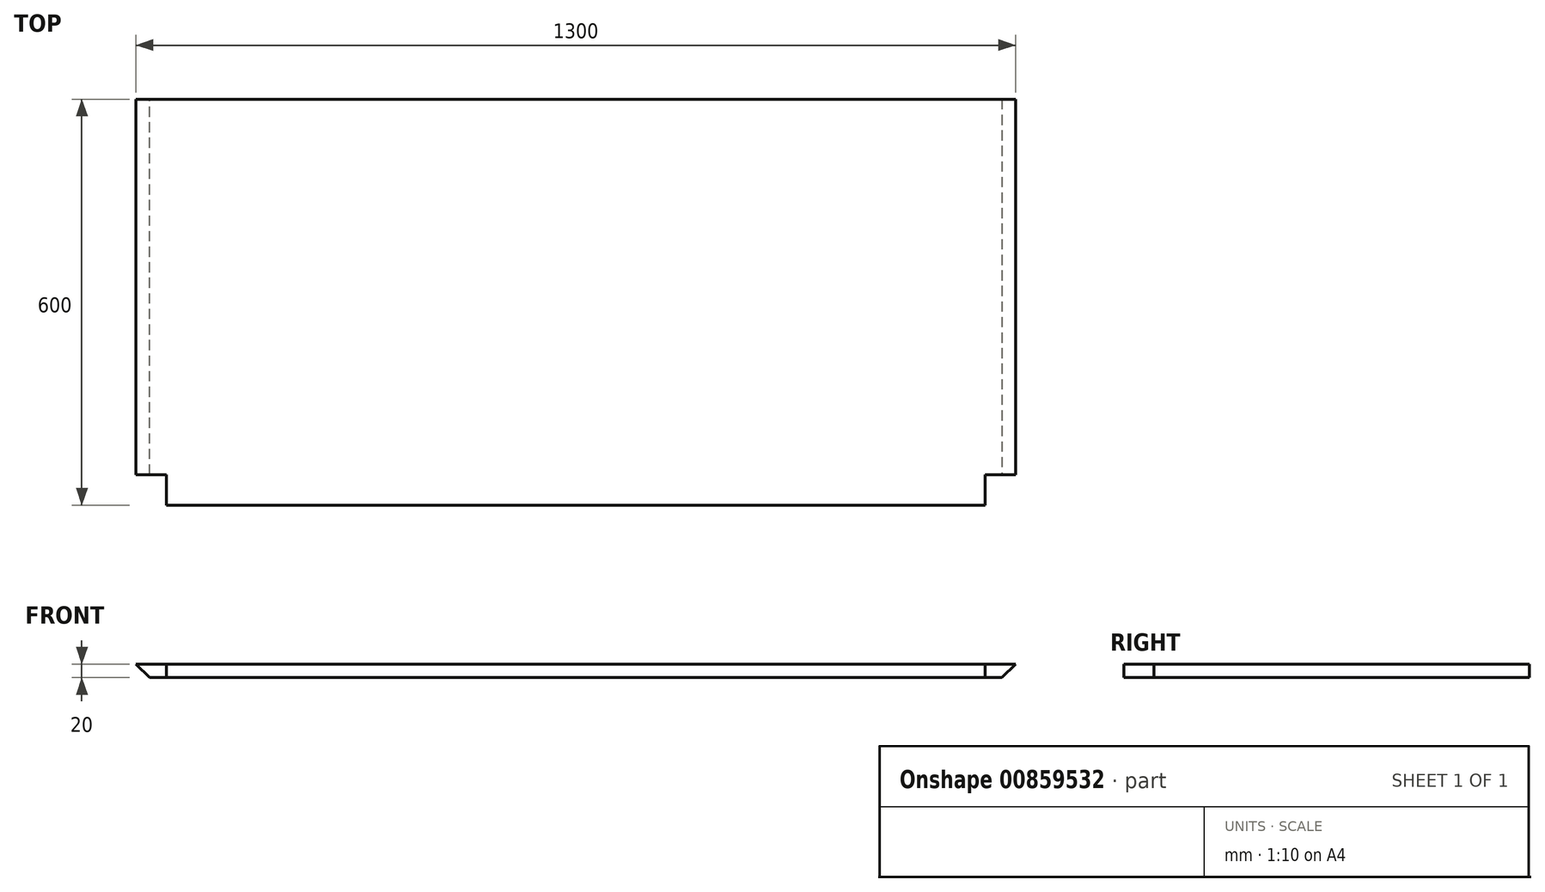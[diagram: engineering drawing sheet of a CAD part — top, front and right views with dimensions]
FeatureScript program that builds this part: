
annotation { "Feature Type Name" : "Feature", "Feature Type Description" : "" }
export const myFeature = defineFeature(function(context is Context, id is Id, definition is map)
    precondition{}
    {
        {
            var Q0;
            Q0=qCreatedBy(makeId("Top.planeOp"),FACE);
            var sketch = newSketch(context, id + "F0", { "sketchPlane" : qUnion([Q0])});
            skLineSegment(sketch, "E0.bottom", {"start": v(-1245.78, 569.46) * mm, "end": v(54.22, 569.46) * mm});
            skLineSegment(sketch, "E0.top", {"start": v(-1245.78, -30.54) * mm, "end": v(54.22, -30.54) * mm});
            skLineSegment(sketch, "E0.left", {"start": v(-1245.78, 569.46) * mm, "end": v(-1245.78, -30.54) * mm});
            skLineSegment(sketch, "E0.right", {"start": v(54.22, 569.46) * mm, "end": v(54.22, -30.54) * mm});
            skLineSegment(sketch, "E1.bottom", {"start": v(-1245.78, -30.54) * mm, "end": v(-1200.78, -30.54) * mm});
            skLineSegment(sketch, "E1.top", {"start": v(-1245.78, 14.46) * mm, "end": v(-1200.78, 14.46) * mm});
            skLineSegment(sketch, "E1.left", {"start": v(-1245.78, -30.54) * mm, "end": v(-1245.78, 14.46) * mm});
            skLineSegment(sketch, "E1.right", {"start": v(-1200.78, -30.54) * mm, "end": v(-1200.78, 14.46) * mm});
            skLineSegment(sketch, "E2.bottom", {"start": v(54.22, -30.54) * mm, "end": v(9.22, -30.54) * mm});
            skLineSegment(sketch, "E2.top", {"start": v(54.22, 14.46) * mm, "end": v(9.22, 14.46) * mm});
            skLineSegment(sketch, "E2.left", {"start": v(54.22, -30.54) * mm, "end": v(54.22, 14.46) * mm});
            skLineSegment(sketch, "E2.right", {"start": v(9.22, -30.54) * mm, "end": v(9.22, 14.46) * mm});
            skSolve(sketch);
        }
        {
            var Q0;
            Q0=makeQuery(id+"F0.imprint","IMPRINT",FACE,{"disambiguationData":[TD([[makeQuery(id+"F0.imprint","IMPRINT",EDGE,{"derivedFrom":sQuery(id+"F0.wireOp",EDGE,"E0.bottom")}),-1.0]])]});
            extrude(context, id + "F1", {"entities" : qUnion([Q0]), "oppositeDirection" : true, "depth" : 20 * mm, "offsetDistance" : 25 * mm});
        }
        {
            var Q0;
            Q0=makeQuery(id+"F1.opExtrude","CAP_EDGE",EDGE,{"disambiguationData":[OSD([sQuery(id+"F0.wireOp",EDGE,"E0.left")])],"isStart":false});
            var Q1;
            Q1=makeQuery(id+"F1.opExtrude","CAP_EDGE",EDGE,{"disambiguationData":[OSD([sQuery(id+"F0.wireOp",EDGE,"E0.right")])],"isStart":false});
            chamfer(context, id + "F2", {"entities" : qUnion([Q0, Q1]), "width" : 20 * mm, "tangentPropagation" : true});
        }
    });
